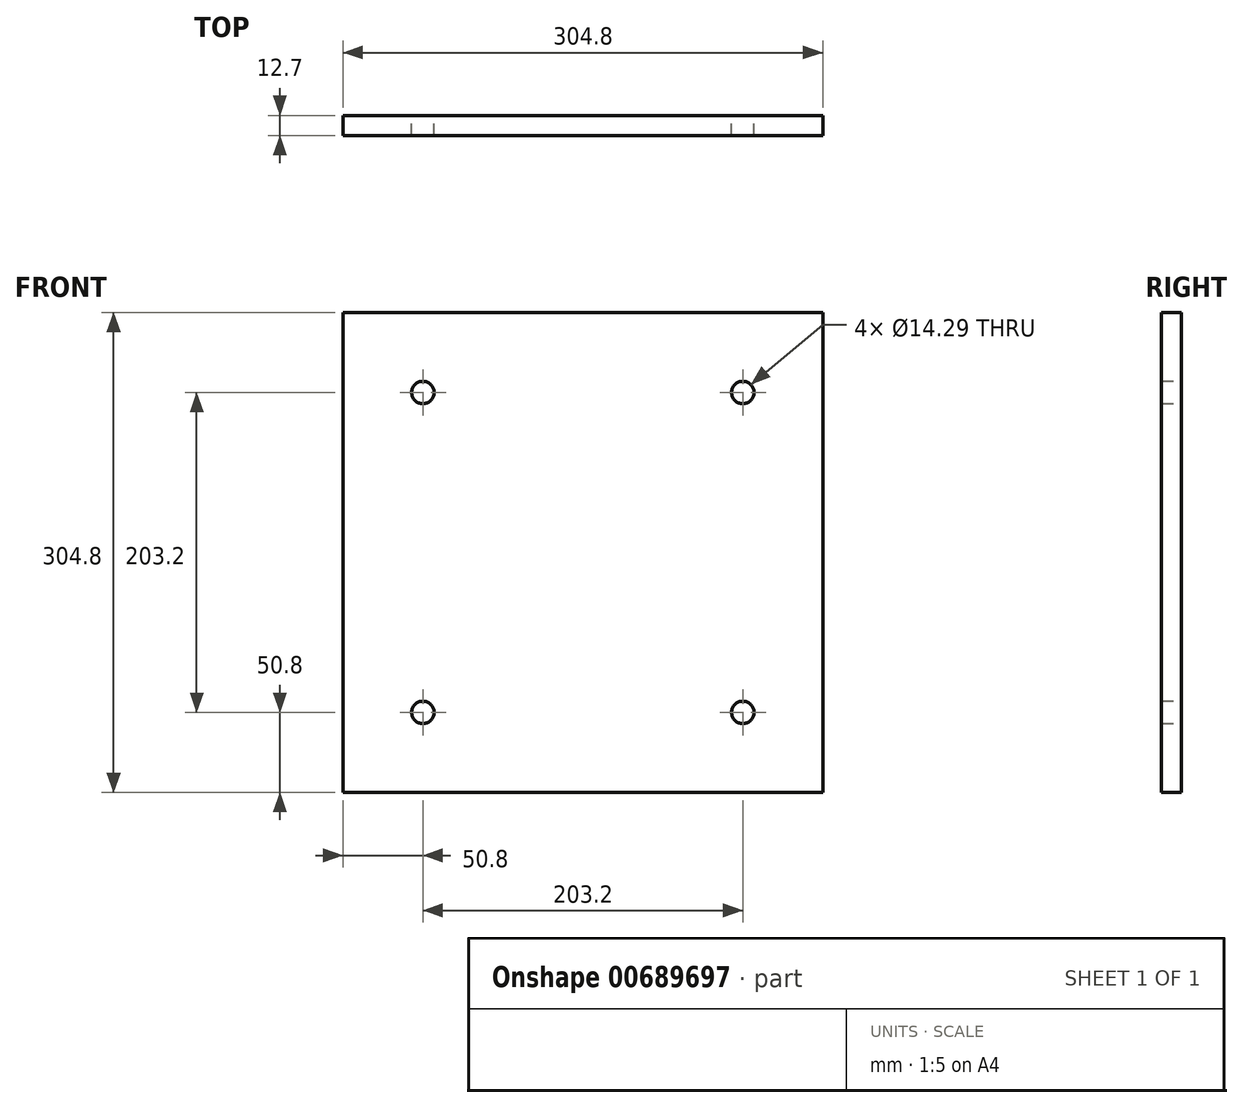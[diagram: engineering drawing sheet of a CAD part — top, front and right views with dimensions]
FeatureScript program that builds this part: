
annotation { "Feature Type Name" : "Feature", "Feature Type Description" : "" }
export const myFeature = defineFeature(function(context is Context, id is Id, definition is map)
    precondition{}
    {
        {
            var Q0;
            Q0=qCreatedBy(makeId("Front.planeOp"),FACE);
            var sketch = newSketch(context, id + "F0", { "sketchPlane" : qUnion([Q0])});
            skLineSegment(sketch, "E0.bottom", {"start": v(152.4, 152.4) * mm, "end": v(-152.4, 152.4) * mm});
            skLineSegment(sketch, "E0.top", {"start": v(152.4, -152.4) * mm, "end": v(-152.4, -152.4) * mm});
            skLineSegment(sketch, "E0.left", {"start": v(152.4, 152.4) * mm, "end": v(152.4, -152.4) * mm});
            skLineSegment(sketch, "E0.right", {"start": v(-152.4, 152.4) * mm, "end": v(-152.4, -152.4) * mm});
            skPoint(sketch, "E0.middle", {"position": v(0, 0) * mm});
            skSolve(sketch);
        }
        {
            var Q0;
            Q0 = qSketchRegion(id + "F0", true);
            extrude(context, id + "F1", {"entities" : qUnion([Q0]), "depth" : 12.7 * mm, "offsetDistance" : 25.4 * mm});
        }
        {
            var Q0;
            Q0=makeQuery(id+"F1.opExtrude","CAP_FACE",FACE,{"disambiguationData":[OSD([sQuery(id+"F0.wireOp",EDGE,"E0.bottom"),sQuery(id+"F0.wireOp",EDGE,"E0.top"),sQuery(id+"F0.wireOp",EDGE,"E0.left"),sQuery(id+"F0.wireOp",EDGE,"E0.right")])],"isStart":true});
            var sketch = newSketch(context, id + "F2", { "sketchPlane" : qUnion([Q0])});
            skLineSegment(sketch, "E1.bottom", {"start": v(101.6, 101.6) * mm, "end": v(-101.6, 101.6) * mm, "construction": true});
            skLineSegment(sketch, "E1.top", {"start": v(101.6, -101.6) * mm, "end": v(-101.6, -101.6) * mm, "construction": true});
            skLineSegment(sketch, "E1.left", {"start": v(101.6, 101.6) * mm, "end": v(101.6, -101.6) * mm, "construction": true});
            skLineSegment(sketch, "E1.right", {"start": v(-101.6, 101.6) * mm, "end": v(-101.6, -101.6) * mm, "construction": true});
            skPoint(sketch, "E1.middle", {"position": v(0, 0) * mm});
            skSolve(sketch);
        }
        {
            var Q0;
            Q0=sQuery(id+"F2.wireOp",VERTEX,"E1.right.start");
            var Q1;
            Q1=sQuery(id+"F2.wireOp",VERTEX,"E1.left.start");
            var Q2;
            Q2=sQuery(id+"F2.wireOp",VERTEX,"E1.left.end");
            var Q3;
            Q3=sQuery(id+"F2.wireOp",VERTEX,"E1.top.end");
            var Q4;
            Q4=makeQuery(id+"F1.opExtrude","SWEPT_BODY",BODY,{"disambiguationData":[OSD([sQuery(id+"F0.wireOp",EDGE,"E0.bottom"),sQuery(id+"F0.wireOp",EDGE,"E0.top"),sQuery(id+"F0.wireOp",EDGE,"E0.left"),sQuery(id+"F0.wireOp",EDGE,"E0.right")])]});
            hole(context, id + "F3", {"style" : HoleStyle.SIMPLE, "endStyle" : HoleEndStyle.THROUGH, "holeDiameter" : 14.29 * mm, "majorDiameter" : 6.35 * mm, "isTappedThrough" : true, "tappedDepth" : 12.7 * mm, "tapClearance" : 3, "startFromSketch" : true, "locations" : qUnion([Q0, Q1, Q2, Q3]), "scope" : qUnion([Q4])});
        }
    });
